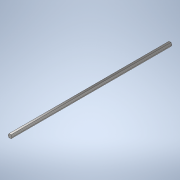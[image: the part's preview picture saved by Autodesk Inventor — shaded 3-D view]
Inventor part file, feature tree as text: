
AUTODESK INVENTOR PART (.ipt)
format: ipt  version: 2020 (Build 240168000, 168)  size: 106,496 bytes
history: native  units: in
note: dims shown in document units (in); Inventor stores cm internally (conversion verified against a paired STEP export)
features: extrude x1, sketch x1
ambient origin geometry x8: Origin, YZ Plane, XZ Plane, XY Plane, X Axis, Y Axis, Z Axis, Center Point
bodies: Solid1 (feature_tree)
feature tree (2):
  extrude  "Extrusion1"  Depth=23.0in TaperAngle=0.0deg
  sketch  "Sketch1"  dims[d0=0.5in d1=23.0in d2=0.0in]
